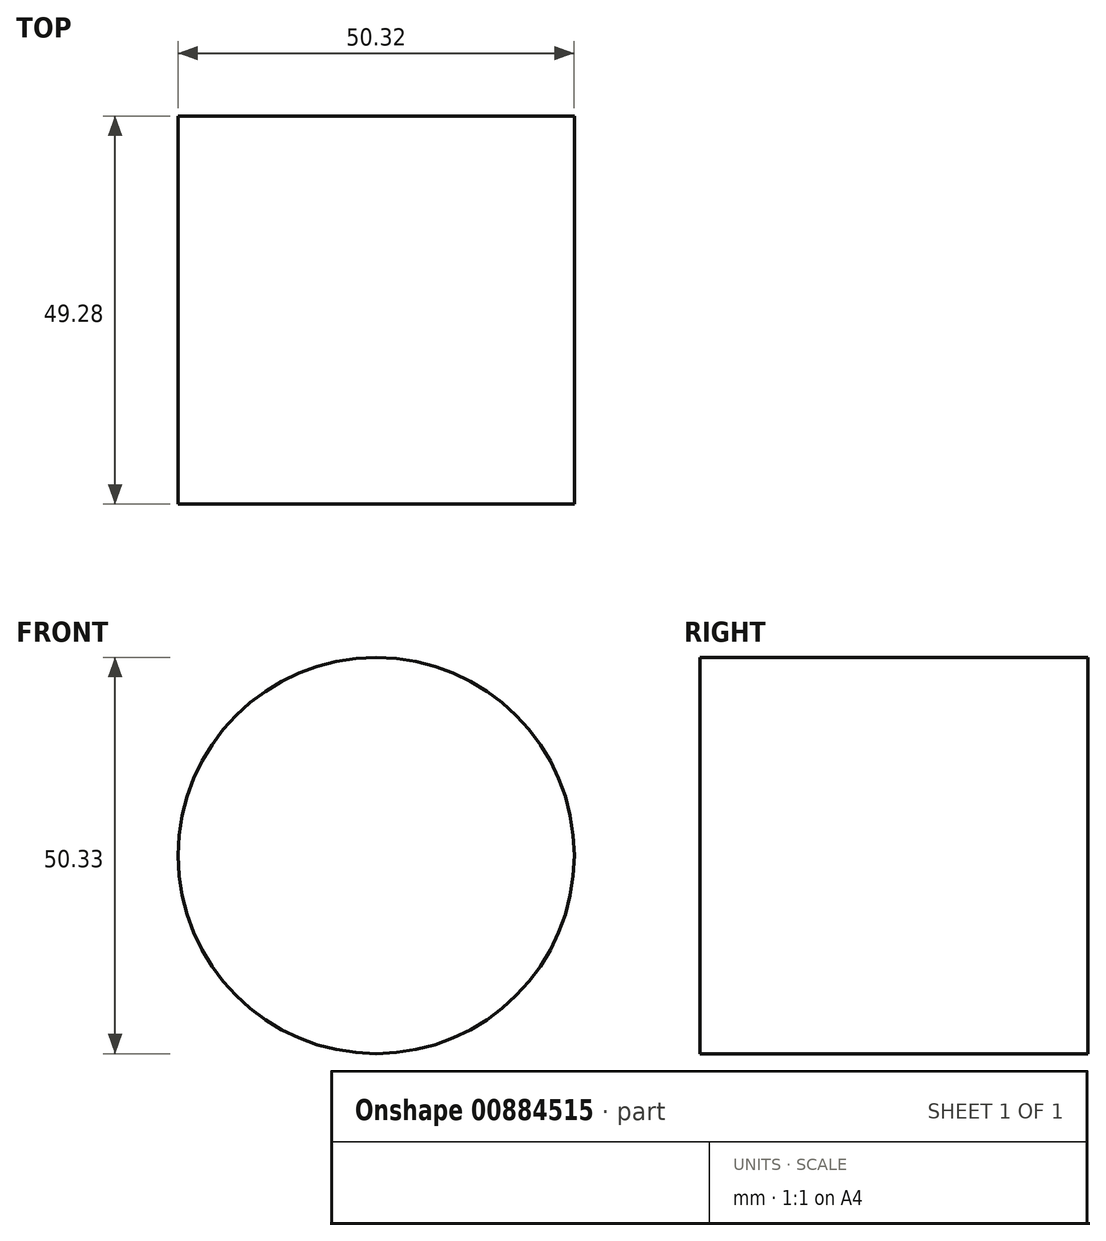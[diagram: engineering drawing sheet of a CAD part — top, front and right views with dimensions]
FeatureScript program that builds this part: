
annotation { "Feature Type Name" : "Feature", "Feature Type Description" : "" }
export const myFeature = defineFeature(function(context is Context, id is Id, definition is map)
    precondition{}
    {
        {
            var Q0;
            Q0=qCreatedBy(makeId("Front.planeOp"),FACE);
            var sketch = newSketch(context, id + "F0", { "sketchPlane" : qUnion([Q0])});
            skCircle(sketch, "E0", {"center": v(-12.7, 13.92) * mm, "radius": 25.16 * mm});
            skSolve(sketch);
        }
        {
            var Q0;
            Q0=makeQuery(id+"F0.imprint","IMPRINT",FACE,{"disambiguationData":[TD([[makeQuery(id+"F0.imprint","IMPRINT",EDGE,{"derivedFrom":sQuery(id+"F0.wireOp",EDGE,"E0")}),1.0]])]});
            extrude(context, id + "F1", {"entities" : qUnion([Q0]), "depth" : 49.28 * mm, "offsetDistance" : 25.4 * mm});
        }
    });
